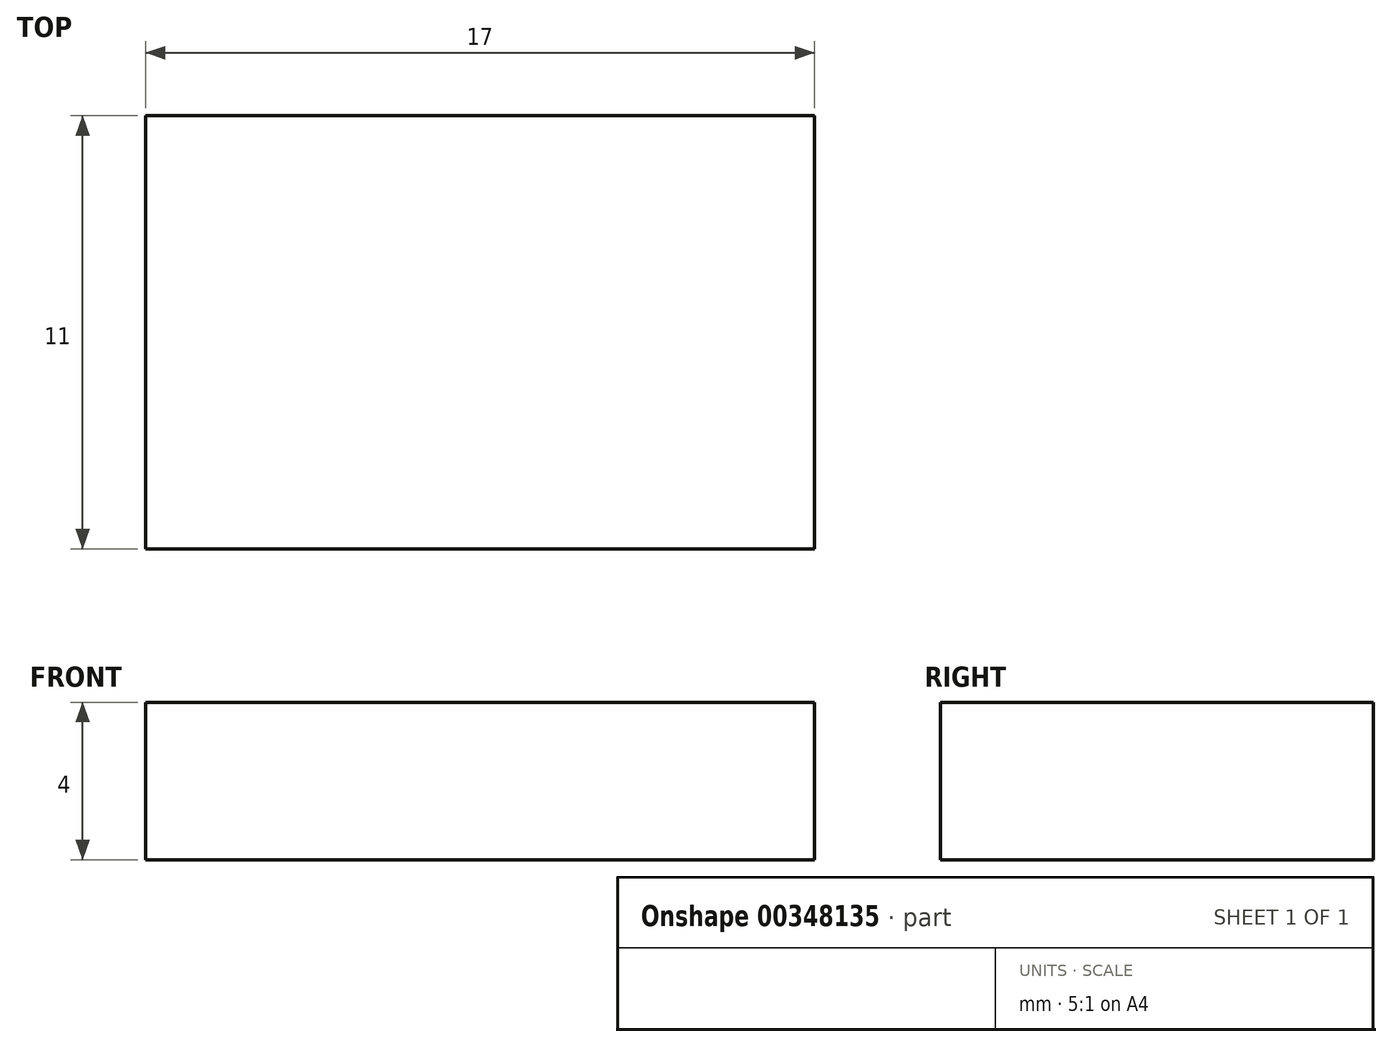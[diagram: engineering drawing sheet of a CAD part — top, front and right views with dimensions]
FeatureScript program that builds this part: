
annotation { "Feature Type Name" : "Feature", "Feature Type Description" : "" }
export const myFeature = defineFeature(function(context is Context, id is Id, definition is map)
    precondition{}
    {
        {
            var Q0;
            Q0=qCreatedBy(makeId("Top.planeOp"),FACE);
            var sketch = newSketch(context, id + "F0", { "sketchPlane" : qUnion([Q0])});
            skLineSegment(sketch, "E0.bottom", {"start": v(8.5, 5.5) * mm, "end": v(-8.5, 5.5) * mm});
            skLineSegment(sketch, "E0.top", {"start": v(8.5, -5.5) * mm, "end": v(-8.5, -5.5) * mm});
            skLineSegment(sketch, "E0.left", {"start": v(8.5, 5.5) * mm, "end": v(8.5, -5.5) * mm});
            skLineSegment(sketch, "E0.right", {"start": v(-8.5, 5.5) * mm, "end": v(-8.5, -5.5) * mm});
            skPoint(sketch, "E0.middle", {"position": v(0, 0) * mm});
            skSolve(sketch);
        }
        {
            var Q0;
            Q0=qCreatedBy(makeId("Front.planeOp"),FACE);
            var sketch = newSketch(context, id + "F1", { "sketchPlane" : qUnion([Q0])});
            skLineSegment(sketch, "E1", {"start": v(0, 0) * mm, "end": v(0, 4) * mm});
            skSolve(sketch);
        }
        {
            var Q0;
            Q0=makeQuery(id+"F0.imprint","IMPRINT",FACE,{"disambiguationData":[TD([[makeQuery(id+"F0.imprint","IMPRINT",EDGE,{"derivedFrom":sQuery(id+"F0.wireOp",EDGE,"E0.bottom")}),1.0]])]});
            var Q1;
            Q1=sQuery(id+"F1.wireOp",EDGE,"E1");
            sweep(context, id + "F2", {"profiles" : qUnion([Q0]), "path" : qUnion([Q1])});
        }
    });
